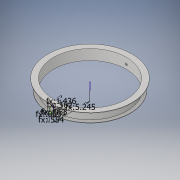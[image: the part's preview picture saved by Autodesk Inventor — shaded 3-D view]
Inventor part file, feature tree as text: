
AUTODESK INVENTOR PART (.ipt)
format: ipt  version: 2017 (Build 210142000, 142)  size: 161,280 bytes
history: native  units: in
note: dims shown in document units (in); Inventor stores cm internally (conversion verified against a paired STEP export)
features: sketch x3, extrude x3, revolve x1, plane x1
ambient origin geometry x8: Origin, YZ Plane, XZ Plane, XY Plane, X Axis, Y Axis, Z Axis, Center Point
bodies: Solid1 (feature_tree)
feature tree (8):
  revolve  "Revolution1"  [1 undecoded]
  plane  "Work Plane1"
  sketch  "Sketch2"  dims[d3=1.4364in d4=0.0625in]
  extrude  "Extrusion2"  Depth=0.0625in
  extrude  "Extrusion3"  TaperAngle=90.0deg  [1 undecoded]
  extrude  "Extrusion4"  Depth=0.0625in
  sketch  "Sketch1"  dims[d1=0.5536in d2=0.0625in]
  sketch  "Sketch3"  dims[d5=0.0625in d6=90.0deg d7=0.562in d8=0.375in d11=0.3125in d12=1.0in d13=0.0in d14=0.0156in d15=0.0in d16=0.25in d17=0.0625in d18=0.0in]
note: 2 required parameter values undecoded (feature->parameter linkage not recoverable at this tier; creation-order binding heuristic only, values carry confidence <= 0.55)